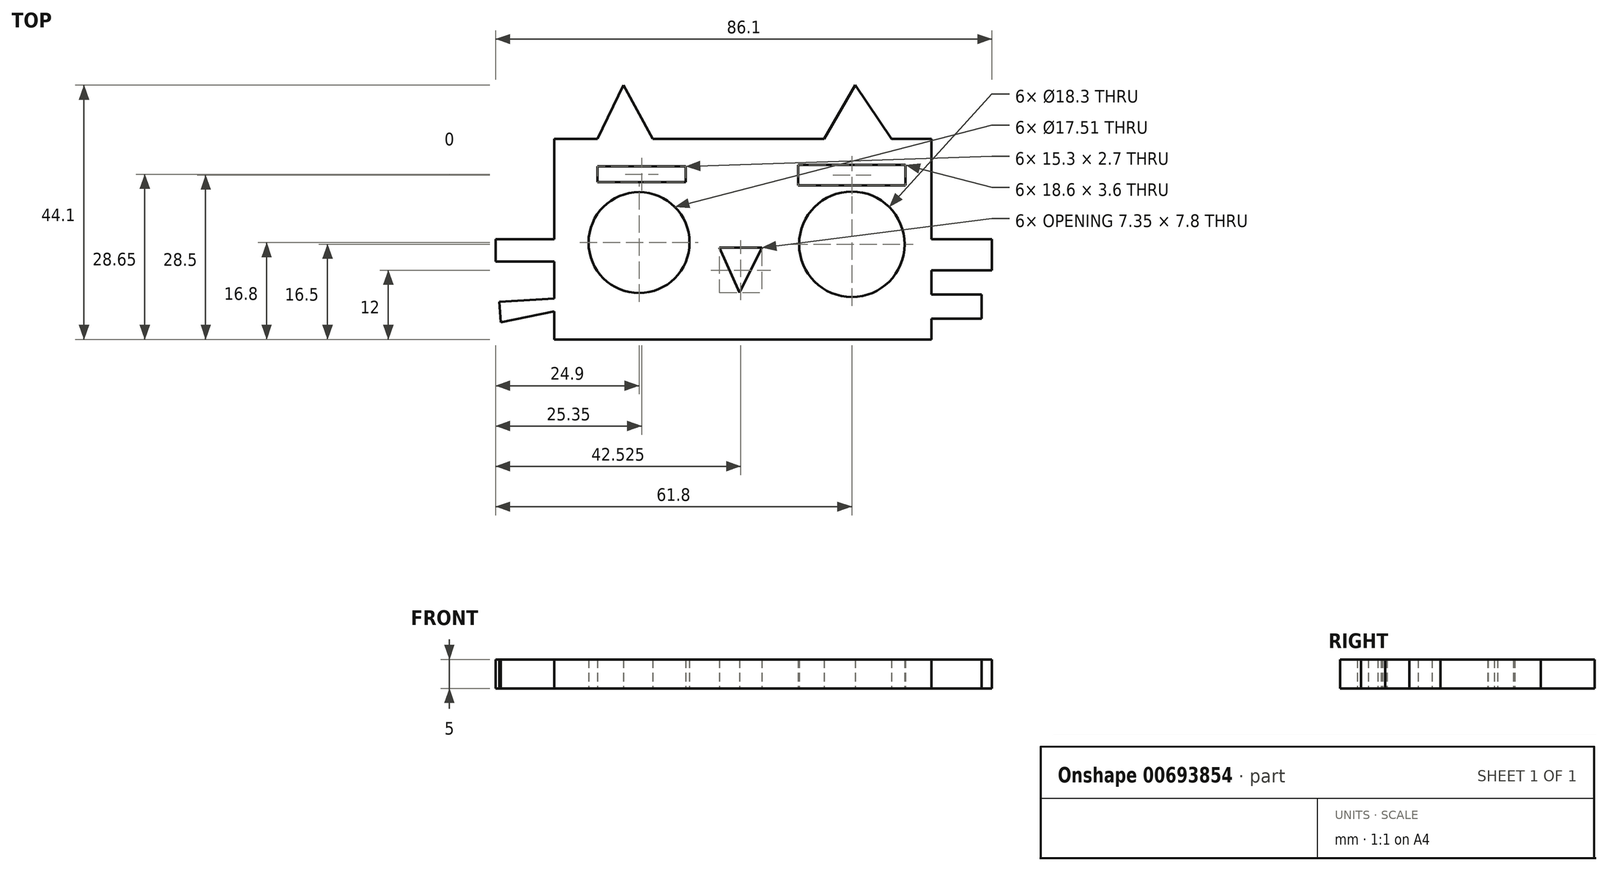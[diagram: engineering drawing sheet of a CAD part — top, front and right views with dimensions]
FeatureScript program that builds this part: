
annotation { "Feature Type Name" : "Feature", "Feature Type Description" : "" }
export const myFeature = defineFeature(function(context is Context, id is Id, definition is map)
    precondition{}
    {
        {
            var Q0;
            Q0=qCreatedBy(makeId("Top.planeOp"),FACE);
            var sketch = newSketch(context, id + "F0", { "sketchPlane" : qUnion([Q0])});
            skLineSegment(sketch, "E0.bottom", {"start": v(-28.65, 43.5) * mm, "end": v(36.75, 43.5) * mm});
            skLineSegment(sketch, "E0.top", {"start": v(-28.65, 8.7) * mm, "end": v(36.75, 8.7) * mm});
            skLineSegment(sketch, "E0.left", {"start": v(-28.65, 43.5) * mm, "end": v(-28.65, 8.7) * mm});
            skLineSegment(sketch, "E0.right", {"start": v(36.75, 43.5) * mm, "end": v(36.75, 8.7) * mm});
            skCircle(sketch, "E1", {"center": v(-13.95, 25.5) * mm, "radius": 8.75 * mm});
            skCircle(sketch, "E2", {"center": v(22.95, 25.2) * mm, "radius": 9.15 * mm});
            skLineSegment(sketch, "E3", {"start": v(0, 24.6) * mm, "end": v(7.35, 24.6) * mm});
            skLineSegment(sketch, "E4", {"start": v(7.35, 24.6) * mm, "end": v(3.45, 16.8) * mm});
            skLineSegment(sketch, "E5", {"start": v(3.45, 16.8) * mm, "end": v(0, 24.6) * mm});
            skLineSegment(sketch, "E6", {"start": v(18.15, 43.5) * mm, "end": v(23.55, 52.8) * mm});
            skLineSegment(sketch, "E7", {"start": v(23.55, 52.8) * mm, "end": v(29.85, 43.5) * mm});
            skLineSegment(sketch, "E8", {"start": v(29.85, 43.5) * mm, "end": v(-11.55, 43.5) * mm});
            skLineSegment(sketch, "E9", {"start": v(-11.55, 43.5) * mm, "end": v(-16.65, 52.8) * mm});
            skLineSegment(sketch, "E10", {"start": v(-16.65, 52.8) * mm, "end": v(-21.15, 43.5) * mm});
            skLineSegment(sketch, "E11", {"start": v(-28.65, 26.1) * mm, "end": v(-38.85, 26.1) * mm});
            skLineSegment(sketch, "E12", {"start": v(-38.85, 26.1) * mm, "end": v(-38.85, 22.2) * mm});
            skLineSegment(sketch, "E13", {"start": v(-38.85, 22.2) * mm, "end": v(-28.65, 22.2) * mm});
            skLineSegment(sketch, "E14", {"start": v(-28.65, 22.2) * mm, "end": v(-28.65, 15.82) * mm});
            skLineSegment(sketch, "E15", {"start": v(-28.65, 15.82) * mm, "end": v(-38.17, 15.22) * mm});
            skLineSegment(sketch, "E16", {"start": v(-38.17, 15.22) * mm, "end": v(-37.95, 11.68) * mm});
            skLineSegment(sketch, "E17", {"start": v(-37.95, 11.68) * mm, "end": v(-28.65, 13.57) * mm});
            skLineSegment(sketch, "E18", {"start": v(36.75, 26.1) * mm, "end": v(47.25, 26.1) * mm});
            skLineSegment(sketch, "E19", {"start": v(47.25, 26.1) * mm, "end": v(47.25, 20.7) * mm});
            skLineSegment(sketch, "E20", {"start": v(47.25, 20.7) * mm, "end": v(36.75, 20.7) * mm});
            skLineSegment(sketch, "E21", {"start": v(36.75, 20.7) * mm, "end": v(36.75, 16.5) * mm});
            skLineSegment(sketch, "E22", {"start": v(36.75, 16.5) * mm, "end": v(45.45, 16.5) * mm});
            skLineSegment(sketch, "E23", {"start": v(45.45, 16.5) * mm, "end": v(45.45, 12.3) * mm});
            skLineSegment(sketch, "E24", {"start": v(45.45, 12.3) * mm, "end": v(36.75, 12.3) * mm});
            skLineSegment(sketch, "E25.bottom", {"start": v(-21.15, 38.7) * mm, "end": v(-5.85, 38.7) * mm});
            skLineSegment(sketch, "E25.top", {"start": v(-21.15, 36) * mm, "end": v(-5.85, 36) * mm});
            skLineSegment(sketch, "E25.left", {"start": v(-21.15, 38.7) * mm, "end": v(-21.15, 36) * mm});
            skLineSegment(sketch, "E25.right", {"start": v(-5.85, 38.7) * mm, "end": v(-5.85, 36) * mm});
            skLineSegment(sketch, "E26.bottom", {"start": v(13.65, 39) * mm, "end": v(32.25, 39) * mm});
            skLineSegment(sketch, "E26.top", {"start": v(13.65, 35.4) * mm, "end": v(32.25, 35.4) * mm});
            skLineSegment(sketch, "E26.left", {"start": v(13.65, 39) * mm, "end": v(13.65, 35.4) * mm});
            skLineSegment(sketch, "E26.right", {"start": v(32.25, 39) * mm, "end": v(32.25, 35.4) * mm});
            skSolve(sketch);
        }
        {
            var Q0;
            Q0 = qSketchRegion(id + "F0", true);
            extrude(context, id + "F1", {"entities" : qUnion([Q0]), "depth" : 5 * mm, "offsetDistance" : 25 * mm});
        }
    });
